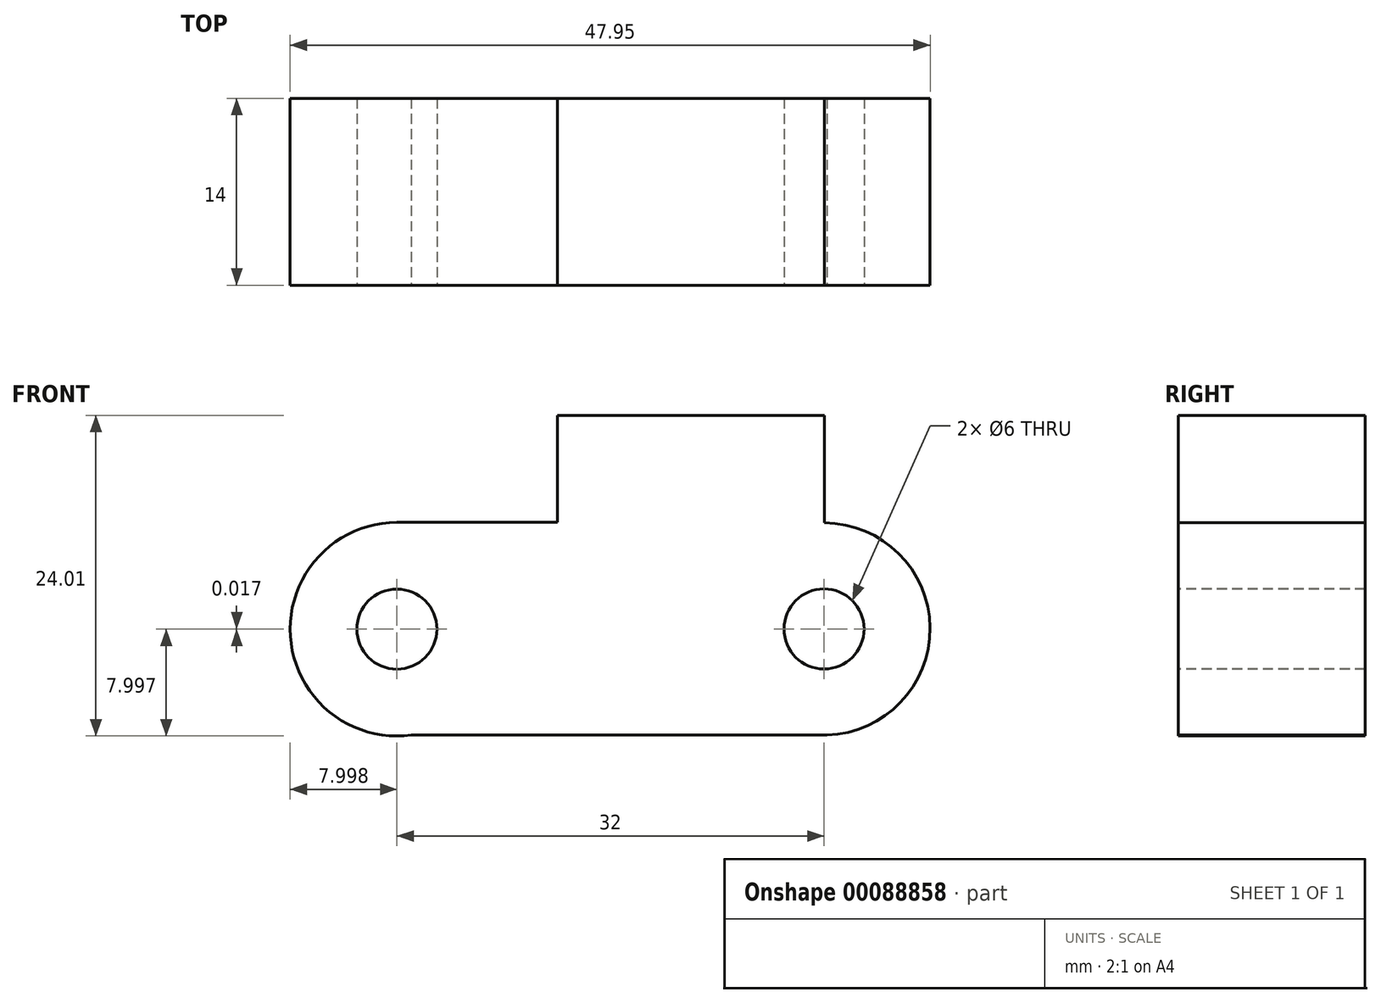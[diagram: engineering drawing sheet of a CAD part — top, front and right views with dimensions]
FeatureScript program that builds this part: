
annotation { "Feature Type Name" : "Feature", "Feature Type Description" : "" }
export const myFeature = defineFeature(function(context is Context, id is Id, definition is map)
    precondition{}
    {
        {
            var Q0;
            Q0=qCreatedBy(makeId("Front.planeOp"),FACE);
            var sketch = newSketch(context, id + "F0", { "sketchPlane" : qUnion([Q0])});
            skLineSegment(sketch, "E0", {"start": v(-15.42, 4) * mm, "end": v(15.72, 4) * mm});
            skLineSegment(sketch, "E1", {"start": v(-16.5, 19.93) * mm, "end": v(-4.48, 19.93) * mm});
            skArc(sketch, "E2", {"start": v(-16.5, 19.93) * mm, "mid": v(-24.47, 11.39) * mm, "end": v(-15.42, 4) * mm});
            skArc(sketch, "E3", {"start": v(15.72, 4) * mm, "mid": v(23.45, 12.04) * mm, "end": v(15.52, 19.9) * mm});
            skLineSegment(sketch, "E4", {"start": v(-4.48, 19.93) * mm, "end": v(-4.48, 27.94) * mm});
            skLineSegment(sketch, "E5", {"start": v(-4.48, 27.94) * mm, "end": v(15.52, 27.94) * mm});
            skLineSegment(sketch, "E6", {"start": v(15.52, 27.94) * mm, "end": v(15.52, 19.9) * mm});
            skCircle(sketch, "E7", {"center": v(-16.5, 11.93) * mm, "radius": 3 * mm});
            skCircle(sketch, "E8", {"center": v(15.5, 11.94) * mm, "radius": 3 * mm});
            skSolve(sketch);
        }
        {
            var Q0;
            Q0 = qSketchRegion(id + "F0", true);
            extrude(context, id + "F1", {"entities" : qUnion([Q0]), "oppositeDirection" : true, "depth" : 14 * mm});
        }
    });
